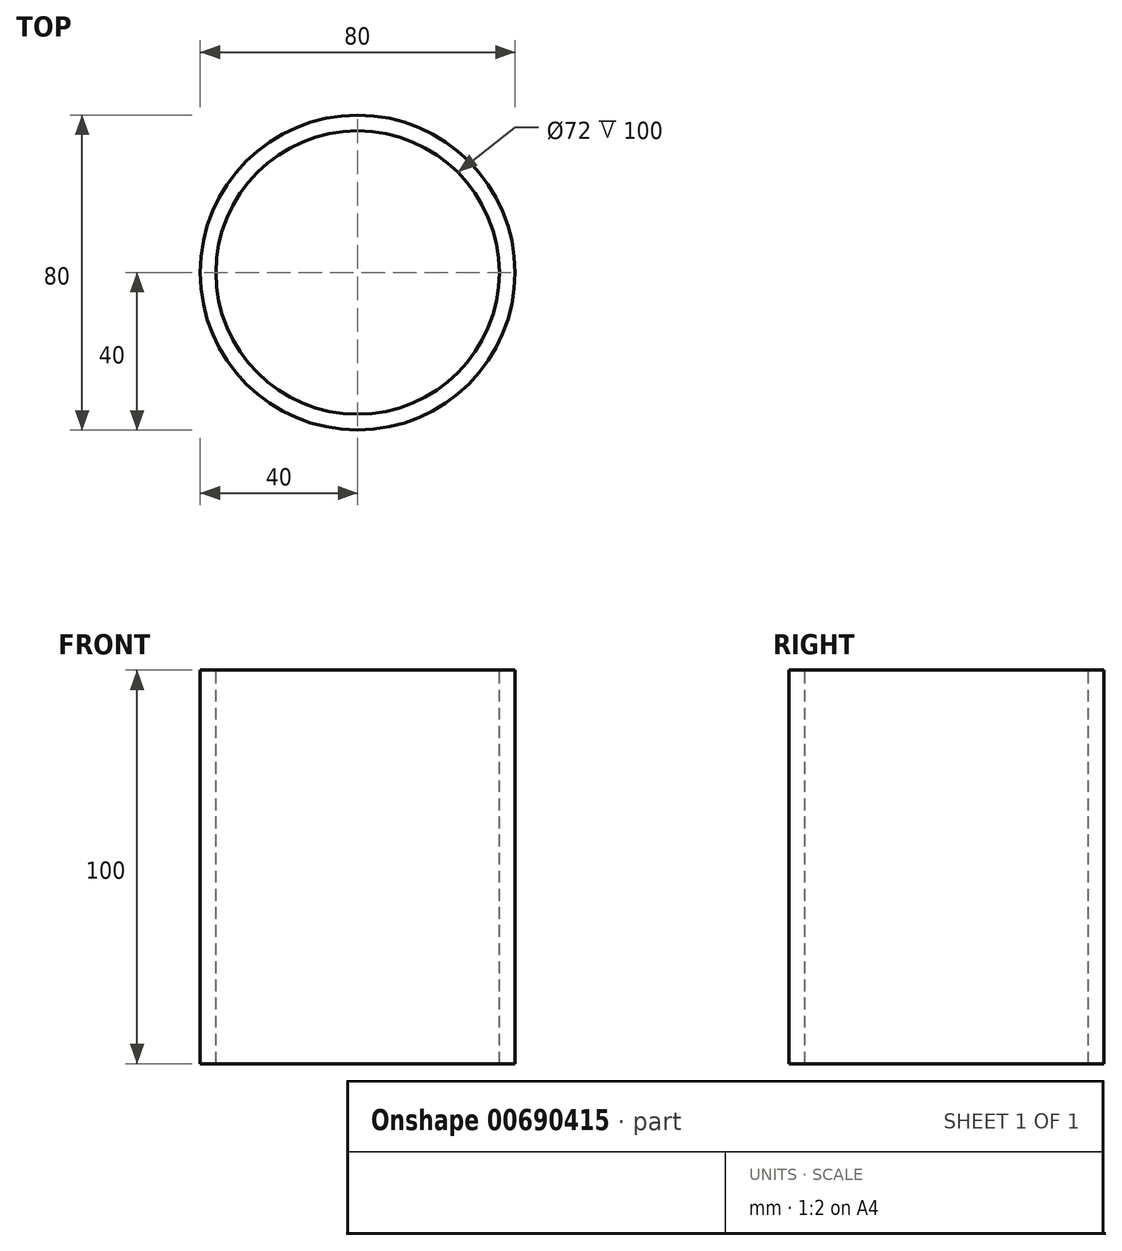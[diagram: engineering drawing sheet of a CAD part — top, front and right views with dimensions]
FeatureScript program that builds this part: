
annotation { "Feature Type Name" : "Feature", "Feature Type Description" : "" }
export const myFeature = defineFeature(function(context is Context, id is Id, definition is map)
    precondition{}
    {
        {
            var Q0;
            Q0=qCreatedBy(makeId("Top.planeOp"),FACE);
            var sketch = newSketch(context, id + "F0", { "sketchPlane" : qUnion([Q0])});
            skCircle(sketch, "E0", {"center": v(0, 0) * mm, "radius": 40 * mm});
            skCircle(sketch, "E1", {"center": v(0, 0) * mm, "radius": 36 * mm});
            skSolve(sketch);
        }
        {
            var Q0;
            Q0=qSketchRegion(id+"F0",true);
            extrude(context, id + "F1", {"entities" : qUnion([Q0]), "oppositeDirection" : true, "depth" : 100 * mm, "offsetDistance" : 25 * mm});
        }
    });
